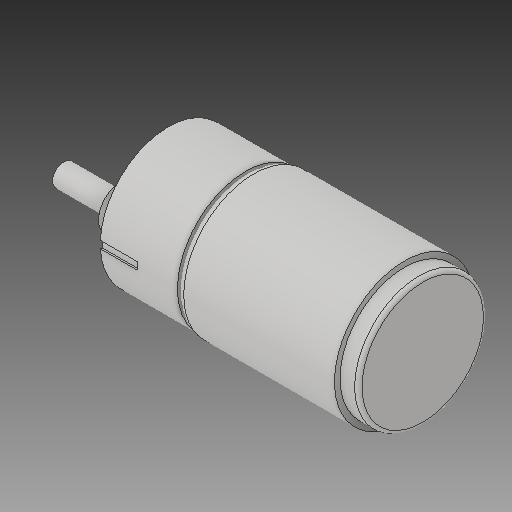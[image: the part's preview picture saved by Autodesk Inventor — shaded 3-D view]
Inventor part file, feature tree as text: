
AUTODESK INVENTOR PART (.ipt)
format: ipt  version: 2019 (Build 230136000, 136)  size: 179,200 bytes
history: native  units: mm
features: extrude x7, sketch x7, fillet x2, other x1
ambient origin geometry x8: Origin, YZ Plane, XZ Plane, XY Plane, X Axis, Y Axis, Z Axis, Center Point
bodies: Body1 (feature_tree)
feature tree (17):
  other  "Твердое тело1"
  extrude  "Выдавливание1"  Depth=37.0mm
  extrude  "Выдавливание2"  Depth=21.0mm TaperAngle=0.0deg
  extrude  "Выдавливание3"  Depth=30.0mm
  fillet  "Сопряжение1"  Radius=0.2mm
  extrude  "Выдавливание4"  Depth=38.0mm
  fillet  "Сопряжение2"  Radius=43.0mm
  extrude  "Выдавливание5"  Depth=2.0mm
  extrude  "Выдавливание6"  Depth=35.0mm
  extrude  "Выдавливание7"  Depth=5.0mm TaperAngle=0.0deg
  sketch  "Эскиз1"
  sketch  "Эскиз2"
  sketch  "Эскиз3"
  sketch  "Эскиз4"
  sketch  "Эскиз5"
  sketch  "Эскиз6"
  sketch  "Эскиз7"
